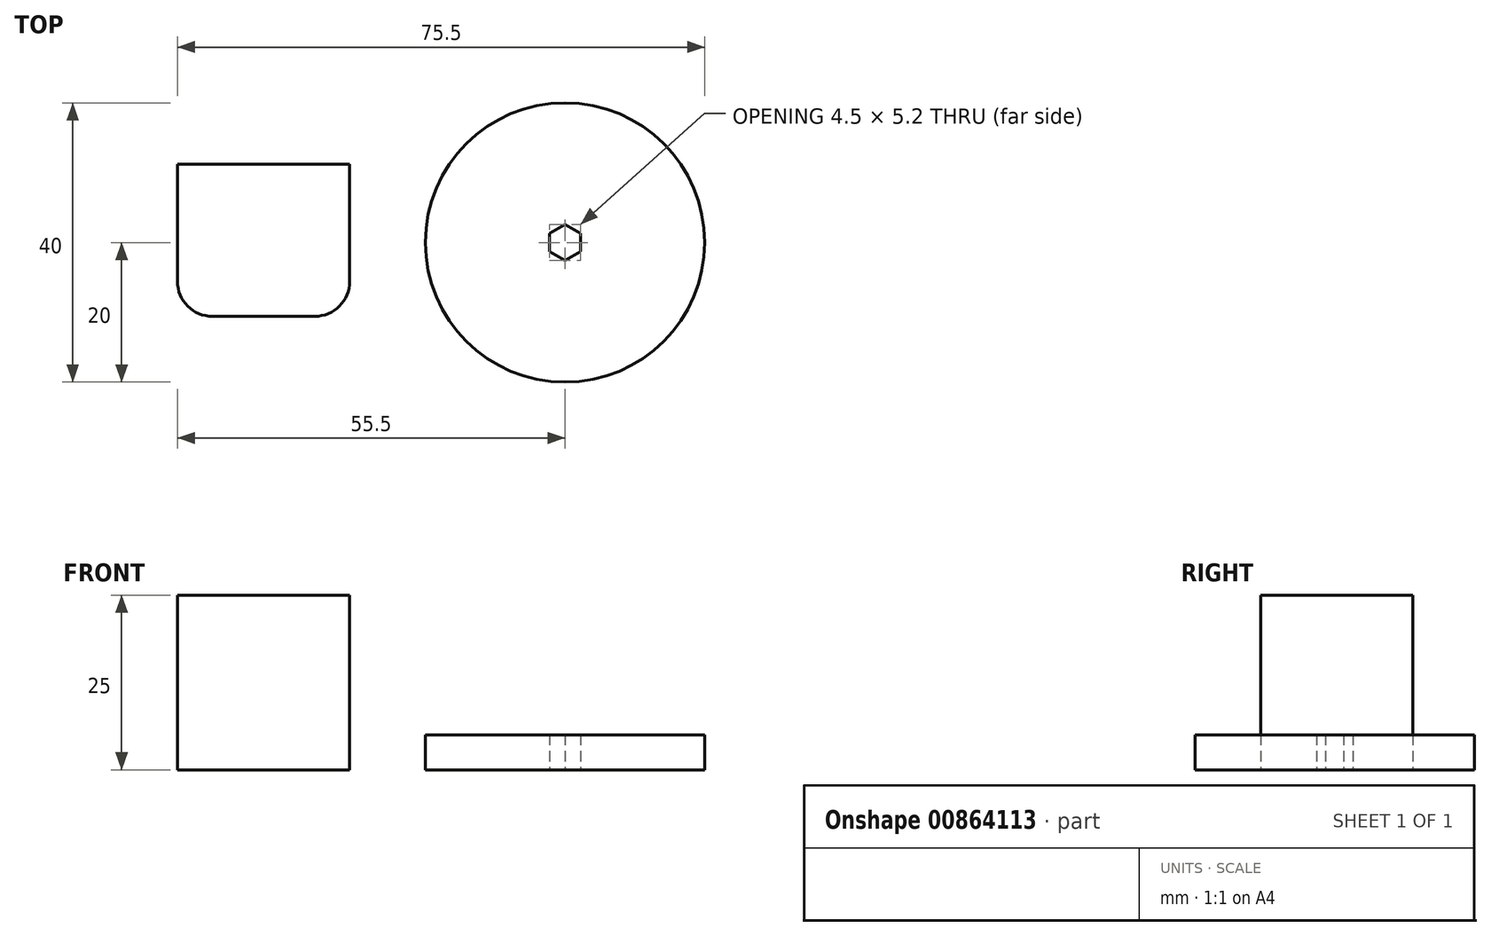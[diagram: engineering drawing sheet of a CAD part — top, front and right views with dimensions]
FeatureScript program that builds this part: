
annotation { "Feature Type Name" : "Feature", "Feature Type Description" : "" }
export const myFeature = defineFeature(function(context is Context, id is Id, definition is map)
    precondition{}
    {
        {
            var Q0;
            Q0=qCreatedBy(makeId("Top.planeOp"),FACE);
            var sketch = newSketch(context, id + "F0", { "sketchPlane" : qUnion([Q0])});
            skCircle(sketch, "E0", {"center": v(0, 0) * mm, "radius": 20 * mm});
            skCircle(sketch, "E1.cCircle", {"center": v(0, 0) * mm, "radius": 2.25 * mm, "construction": true});
            skLineSegment(sketch, "E1.0", {"start": v(2.25, 1.3) * mm, "end": v(2.25, -1.3) * mm});
            skLineSegment(sketch, "E1.1", {"start": v(2.25, -1.3) * mm, "end": v(0, -2.6) * mm});
            skLineSegment(sketch, "E1.2", {"start": v(0, -2.6) * mm, "end": v(-2.25, -1.3) * mm});
            skLineSegment(sketch, "E1.3", {"start": v(-2.25, -1.3) * mm, "end": v(-2.25, 1.3) * mm});
            skLineSegment(sketch, "E1.4", {"start": v(-2.25, 1.3) * mm, "end": v(0, 2.6) * mm});
            skLineSegment(sketch, "E1.5", {"start": v(0, 2.6) * mm, "end": v(2.25, 1.3) * mm});
            skPoint(sketch, "E1.0.midPoint", {"position": v(2.25, 0) * mm});
            skLineSegment(sketch, "E2.bottom", {"start": v(-55.5, 11.18) * mm, "end": v(-30.84, 11.18) * mm});
            skLineSegment(sketch, "E2.top", {"start": v(-55.5, -10.58) * mm, "end": v(-30.84, -10.58) * mm});
            skLineSegment(sketch, "E2.left", {"start": v(-55.5, 11.18) * mm, "end": v(-55.5, -10.58) * mm});
            skLineSegment(sketch, "E2.right", {"start": v(-30.84, 11.18) * mm, "end": v(-30.84, -10.58) * mm});
            skSolve(sketch);
        }
        {
            var Q0;
            Q0=makeQuery(id+"F0.imprint","IMPRINT",FACE,{"disambiguationData":[TD([[makeQuery(id+"F0.imprint","IMPRINT",EDGE,{"derivedFrom":sQuery(id+"F0.wireOp",EDGE,"E0")}),1.0]])]});
            extrude(context, id + "F1", {"entities" : qUnion([Q0]), "depth" : 5 * mm, "offsetDistance" : 25 * mm});
        }
        {
            var Q0;
            Q0=makeQuery(id+"F0.imprint","IMPRINT",FACE,{"disambiguationData":[TD([[makeQuery(id+"F0.imprint","IMPRINT",EDGE,{"derivedFrom":sQuery(id+"F0.wireOp",EDGE,"E2.bottom")}),-1.0]])]});
            extrude(context, id + "F2", {"entities" : qUnion([Q0]), "depth" : 25 * mm, "offsetDistance" : 25 * mm});
        }
        {
            var Q0;
            Q0=makeQuery(id+"F2.opExtrude","SWEPT_EDGE",EDGE,{"disambiguationData":[OSD([sQuery(id+"F0.wireOp",EDGE,"E2.top"),sQuery(id+"F0.wireOp",EDGE,"E2.right")])]});
            var Q1;
            Q1=makeQuery(id+"F2.opExtrude","SWEPT_EDGE",EDGE,{"disambiguationData":[OSD([sQuery(id+"F0.wireOp",EDGE,"E2.top"),sQuery(id+"F0.wireOp",EDGE,"E2.left")])]});
            fillet(context, id + "F3", {"entities" : qUnion([Q0, Q1]), "radius" : 5 * mm, "tangentPropagation" : true, "allowEdgeOverflow" : false});
        }
    });
